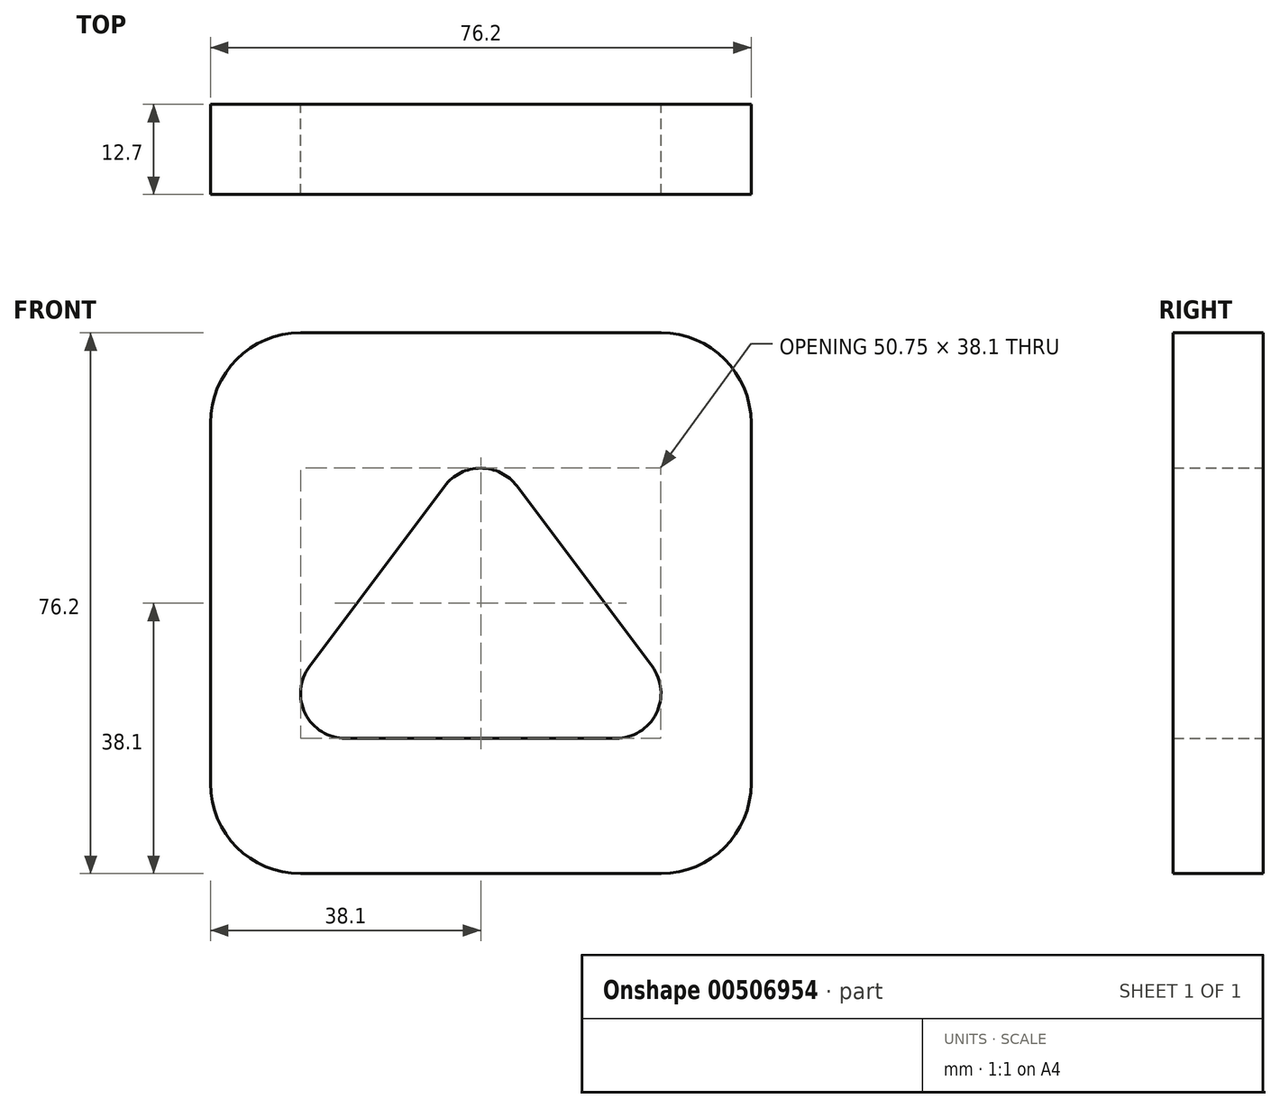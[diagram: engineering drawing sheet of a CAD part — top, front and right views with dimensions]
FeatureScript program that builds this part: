
annotation { "Feature Type Name" : "Feature", "Feature Type Description" : "" }
export const myFeature = defineFeature(function(context is Context, id is Id, definition is map)
    precondition{}
    {
        {
            var Q0;
            Q0=qCreatedBy(makeId("Front.planeOp"),FACE);
            var sketch = newSketch(context, id + "F0", { "sketchPlane" : qUnion([Q0])});
            skLineSegment(sketch, "E0", {"start": v(12.7, 0) * mm, "end": v(63.5, 0) * mm});
            skArc(sketch, "E1", {"start": v(13.97, 29.21) * mm, "mid": v(13.37, 22.56) * mm, "end": v(19.05, 19.05) * mm});
            skArc(sketch, "E2", {"start": v(57.15, 19.05) * mm, "mid": v(62.83, 22.56) * mm, "end": v(62.23, 29.21) * mm});
            skArc(sketch, "E3", {"start": v(43.18, 54.6) * mm, "mid": v(38.1, 57.15) * mm, "end": v(33.02, 54.6) * mm});
            skLineSegment(sketch, "E4", {"start": v(33.02, 54.6) * mm, "end": v(13.97, 29.21) * mm});
            skLineSegment(sketch, "E5", {"start": v(43.18, 54.6) * mm, "end": v(62.23, 29.21) * mm});
            skPoint(sketch, "E6.visualSharp", {"position": v(0, 76.2) * mm});
            skPoint(sketch, "E7.visualSharp", {"position": v(76.2, 76.2) * mm});
            skLineSegment(sketch, "E8", {"start": v(0, 12.7) * mm, "end": v(0, 63.5) * mm});
            skLineSegment(sketch, "E9", {"start": v(63.5, 76.2) * mm, "end": v(12.7, 76.2) * mm});
            skLineSegment(sketch, "E10", {"start": v(76.2, 63.5) * mm, "end": v(76.2, 12.7) * mm});
            skLineSegment(sketch, "E11", {"start": v(19.05, 19.05) * mm, "end": v(57.15, 19.05) * mm});
            skArc(sketch, "E12", {"start": v(12.7, 76.2) * mm, "mid": v(3.72, 72.48) * mm, "end": v(0, 63.5) * mm});
            skArc(sketch, "E13", {"start": v(76.2, 63.5) * mm, "mid": v(72.48, 72.48) * mm, "end": v(63.5, 76.2) * mm});
            skArc(sketch, "E14", {"start": v(0, 12.7) * mm, "mid": v(3.72, 3.72) * mm, "end": v(12.7, 0) * mm});
            skPoint(sketch, "E15.orphan", {"position": v(0, 0) * mm});
            skArc(sketch, "E16", {"start": v(63.5, 0) * mm, "mid": v(72.48, 3.72) * mm, "end": v(76.2, 12.7) * mm});
            skPoint(sketch, "E17.orphan", {"position": v(76.2, 0) * mm});
            skSolve(sketch);
        }
        {
            var Q0;
            Q0=makeQuery(id+"F0.imprint","IMPRINT",FACE,{"disambiguationData":[TD([[makeQuery(id+"F0.imprint","IMPRINT",EDGE,{"derivedFrom":sQuery(id+"F0.wireOp",EDGE,"E0")}),1.0]])]});
            extrude(context, id + "F1", {"entities" : qUnion([Q0]), "depth" : 12.7 * mm});
        }
    });
